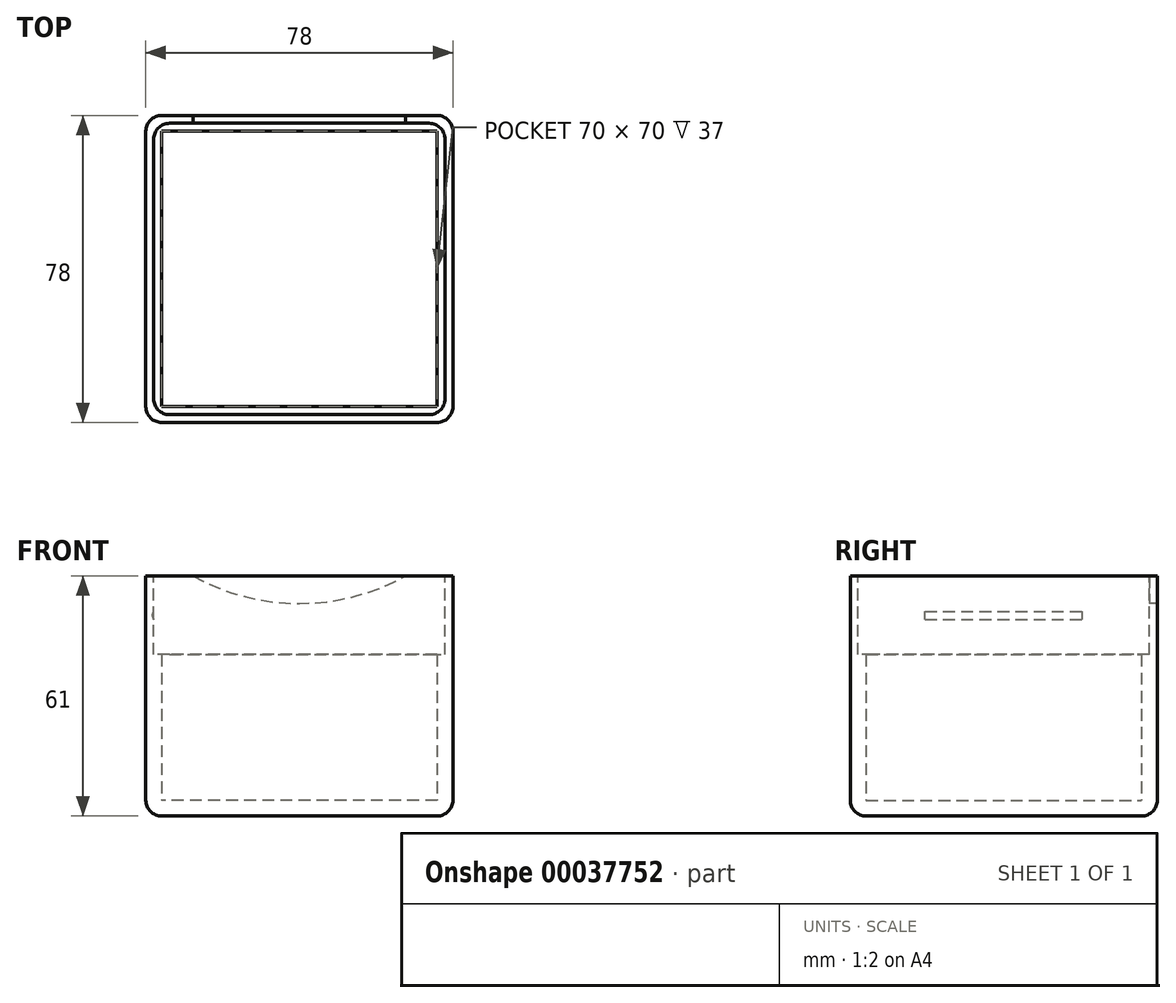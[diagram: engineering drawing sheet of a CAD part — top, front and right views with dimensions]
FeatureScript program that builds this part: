
annotation { "Feature Type Name" : "Feature", "Feature Type Description" : "" }
export const myFeature = defineFeature(function(context is Context, id is Id, definition is map)
    precondition{}
    {
        {
            var Q0;
            Q0=qCreatedBy(makeId("Top.planeOp"),FACE);
            var sketch = newSketch(context, id + "F0", { "sketchPlane" : qUnion([Q0])});
            skLineSegment(sketch, "E0.rect.bottom", {"start": v(39, -39) * mm, "end": v(-39, -39) * mm});
            skLineSegment(sketch, "E0.rect.top", {"start": v(39, 39) * mm, "end": v(-39, 39) * mm});
            skLineSegment(sketch, "E0.rect.left", {"start": v(39, -39) * mm, "end": v(39, 39) * mm});
            skLineSegment(sketch, "E0.rect.right", {"start": v(-39, -39) * mm, "end": v(-39, 39) * mm});
            skPoint(sketch, "E0.rect.middle", {"position": v(0, 0) * mm});
            skSolve(sketch);
        }
        {
            var Q0;
            Q0 = qSketchRegion(id + "F0", true);
            extrude(context, id + "F1", {"entities" : qUnion([Q0]), "depth" : 61 * mm});
        }
        {
            var Q0;
            Q0=makeQuery(id+"F1.opExtrude","CAP_FACE",FACE,{"disambiguationData":[OSD([sQuery(id+"F0.wireOp",EDGE,"E0.rect.bottom"),sQuery(id+"F0.wireOp",EDGE,"E0.rect.top"),sQuery(id+"F0.wireOp",EDGE,"E0.rect.left"),sQuery(id+"F0.wireOp",EDGE,"E0.rect.right")])],"isStart":false});
            shell(context, id + "F2", {"entities" : qUnion([Q0]), "thickness" : 4 * mm});
        }
        {
            var Q0;
            Q0=makeQuery(id+"F1.opExtrude","CAP_FACE",FACE,{"disambiguationData":[OSD([sQuery(id+"F0.wireOp",EDGE,"E0.rect.bottom"),sQuery(id+"F0.wireOp",EDGE,"E0.rect.top"),sQuery(id+"F0.wireOp",EDGE,"E0.rect.left"),sQuery(id+"F0.wireOp",EDGE,"E0.rect.right")])],"isStart":false});
            var sketch = newSketch(context, id + "F3", { "sketchPlane" : qUnion([Q0])});
            skLineSegment(sketch, "E1.rect.bottom", {"start": v(-37, 37) * mm, "end": v(37, 37) * mm});
            skLineSegment(sketch, "E1.rect.top", {"start": v(-37, -37) * mm, "end": v(37, -37) * mm});
            skLineSegment(sketch, "E1.rect.left", {"start": v(-37, 37) * mm, "end": v(-37, -37) * mm});
            skLineSegment(sketch, "E1.rect.right", {"start": v(37, 37) * mm, "end": v(37, -37) * mm});
            skPoint(sketch, "E1.rect.middle", {"position": v(0, 0) * mm});
            skSolve(sketch);
        }
        {
            var Q0;
            Q0=makeQuery(id+"F3.imprint","IMPRINT",FACE,{"disambiguationData":[TD([[makeQuery(id+"F3.imprint","IMPRINT",EDGE,{"derivedFrom":sQuery(id+"F3.wireOp",EDGE,"E1.rect.bottom")}),-1.0]])]});
            extrude(context, id + "F4", {"entities" : qUnion([Q0]), "operationType" : NewBodyOperationType.REMOVE, "oppositeDirection" : true, "depth" : 20 * mm});
        }
        {
            var Q0;
            Q0=makeQuery(id+"F4.boolean.opBoolean","COPY",FACE,{"derivedFrom":makeQuery(id+"F4.opExtrude","SWEPT_FACE",FACE,{"disambiguationData":[OSD([sQuery(id+"F3.wireOp",EDGE,"E1.rect.bottom")])]})});
            var sketch = newSketch(context, id + "F5", { "sketchPlane" : qUnion([Q0])});
            skLineSegment(sketch, "E2", {"start": v(-27, 41) * mm, "end": v(-27, 61) * mm, "construction": true});
            skLineSegment(sketch, "E3", {"start": v(27, 41) * mm, "end": v(27, 61) * mm, "construction": true});
            skArc(sketch, "E4", {"start": v(-27, 61) * mm, "mid": v(0, 54) * mm, "end": v(27, 61) * mm});
            skLineSegment(sketch, "E5", {"start": v(0, 54) * mm, "end": v(0, 61) * mm, "construction": true});
            skSolve(sketch);
        }
        {
            var Q0;
            {var subQ1=sQuery(id+"F5.wireOp",EDGE,"E4");Q0=makeQuery(id+"F5.imprint","IMPRINT",FACE,{"disambiguationData":[TD([[makeQuery(id+"F5.imprint","IMPRINT",EDGE,{"derivedFrom":subQ1}),1.0]])]});}
            extrude(context, id + "F6", {"entities" : qUnion([Q0]), "operationType" : NewBodyOperationType.REMOVE, "oppositeDirection" : true, "depth" : 2 * mm});
        }
        {
            var Q0;
            Q0=makeQuery(id+"F1.opExtrude","SWEPT_EDGE",EDGE,{"disambiguationData":[OSD([sQuery(id+"F0.wireOp",EDGE,"E0.rect.top"),sQuery(id+"F0.wireOp",EDGE,"E0.rect.right")])]});
            var Q1;
            Q1=makeQuery(id+"F1.opExtrude","SWEPT_EDGE",EDGE,{"disambiguationData":[OSD([sQuery(id+"F0.wireOp",EDGE,"E0.rect.top"),sQuery(id+"F0.wireOp",EDGE,"E0.rect.left")])]});
            var Q2;
            Q2=makeQuery(id+"F1.opExtrude","SWEPT_EDGE",EDGE,{"disambiguationData":[OSD([sQuery(id+"F0.wireOp",EDGE,"E0.rect.bottom"),sQuery(id+"F0.wireOp",EDGE,"E0.rect.left")])]});
            var Q3;
            Q3=makeQuery(id+"F1.opExtrude","SWEPT_EDGE",EDGE,{"disambiguationData":[OSD([sQuery(id+"F0.wireOp",EDGE,"E0.rect.bottom"),sQuery(id+"F0.wireOp",EDGE,"E0.rect.right")])]});
            var Q4;
            Q4=makeQuery(id+"F1.opExtrude","CAP_EDGE",EDGE,{"disambiguationData":[OSD([sQuery(id+"F0.wireOp",EDGE,"E0.rect.right")])],"isStart":true});
            var Q5;
            Q5=makeQuery(id+"F1.opExtrude","CAP_EDGE",EDGE,{"disambiguationData":[OSD([sQuery(id+"F0.wireOp",EDGE,"E0.rect.bottom")])],"isStart":true});
            var Q6;
            Q6=makeQuery(id+"F1.opExtrude","CAP_EDGE",EDGE,{"disambiguationData":[OSD([sQuery(id+"F0.wireOp",EDGE,"E0.rect.left")])],"isStart":true});
            var Q7;
            Q7=makeQuery(id+"F1.opExtrude","CAP_EDGE",EDGE,{"disambiguationData":[OSD([sQuery(id+"F0.wireOp",EDGE,"E0.rect.top")])],"isStart":true});
            fillet(context, id + "F7", {"entities" : qUnion([Q0, Q1, Q2, Q3, Q4, Q5, Q6, Q7]), "radius" : 4 * mm, "tangentPropagation" : true, "allowEdgeOverflow" : false});
        }
        {
            var Q0;
            Q0=makeQuery(id+"F4.boolean.opBoolean","COPY",EDGE,{"derivedFrom":makeQuery(id+"F4.opExtrude","SWEPT_EDGE",EDGE,{"disambiguationData":[OSD([sQuery(id+"F3.wireOp",EDGE,"E1.rect.top"),sQuery(id+"F3.wireOp",EDGE,"E1.rect.right")])]})});
            var Q1;
            Q1=makeQuery(id+"F4.boolean.opBoolean","COPY",EDGE,{"derivedFrom":makeQuery(id+"F4.opExtrude","SWEPT_EDGE",EDGE,{"disambiguationData":[OSD([sQuery(id+"F3.wireOp",EDGE,"E1.rect.top"),sQuery(id+"F3.wireOp",EDGE,"E1.rect.left")])]})});
            var Q2;
            Q2=makeQuery(id+"F4.boolean.opBoolean","COPY",EDGE,{"derivedFrom":makeQuery(id+"F4.opExtrude","SWEPT_EDGE",EDGE,{"disambiguationData":[OSD([sQuery(id+"F3.wireOp",EDGE,"E1.rect.bottom"),sQuery(id+"F3.wireOp",EDGE,"E1.rect.right")])]})});
            var Q3;
            Q3=makeQuery(id+"F4.boolean.opBoolean","COPY",EDGE,{"derivedFrom":makeQuery(id+"F4.opExtrude","SWEPT_EDGE",EDGE,{"disambiguationData":[OSD([sQuery(id+"F3.wireOp",EDGE,"E1.rect.bottom"),sQuery(id+"F3.wireOp",EDGE,"E1.rect.left")])]})});
            fillet(context, id + "F8", {"entities" : qUnion([Q0, Q1, Q2, Q3]), "radius" : 4 * mm, "tangentPropagation" : true, "allowEdgeOverflow" : false});
        }
        {
            var Q0;
            Q0=makeQuery(id+"F4.boolean.opBoolean","COPY",FACE,{"derivedFrom":makeQuery(id+"F4.opExtrude","SWEPT_FACE",FACE,{"disambiguationData":[OSD([sQuery(id+"F3.wireOp",EDGE,"E1.rect.left")])]})});
            var sketch = newSketch(context, id + "F9", { "sketchPlane" : qUnion([Q0])});
            skLineSegment(sketch, "E6", {"start": v(-33, 51) * mm, "end": v(33, 51) * mm, "construction": true});
            skLineSegment(sketch, "E7", {"start": v(-20, 50) * mm, "end": v(20, 50) * mm});
            skLineSegment(sketch, "E8.MirrorCS", {"start": v(-20, 52) * mm, "end": v(20, 52) * mm});
            skLineSegment(sketch, "E9", {"start": v(-20, 50) * mm, "end": v(-20, 52) * mm});
            skLineSegment(sketch, "E10", {"start": v(20, 50) * mm, "end": v(20, 52) * mm});
            skSolve(sketch);
        }
        {
            var Q0;
            Q0 = qSketchRegion(id + "F9", true);
            extrude(context, id + "F10", {"entities" : qUnion([Q0]), "operationType" : NewBodyOperationType.REMOVE, "oppositeDirection" : true, "depth" : 0.3 * mm});
        }
        {
            var Q0;
            Q0=makeQuery(id+"F10.boolean.opBoolean","COPY",EDGE,{"derivedFrom":makeQuery(id+"F10.opExtrude","CAP_EDGE",EDGE,{"disambiguationData":[OSD([sQuery(id+"F9.wireOp",EDGE,"E7")])],"isStart":false})});
            var Q1;
            Q1=makeQuery(id+"F10.boolean.opBoolean","COPY",EDGE,{"derivedFrom":makeQuery(id+"F10.opExtrude","CAP_EDGE",EDGE,{"disambiguationData":[OSD([sQuery(id+"F9.wireOp",EDGE,"E8.MirrorCS")])],"isStart":false})});
            fillet(context, id + "F11", {"entities" : qUnion([Q0, Q1]), "radius" : 1 * mm, "tangentPropagation" : true, "allowEdgeOverflow" : false});
        }
    });
